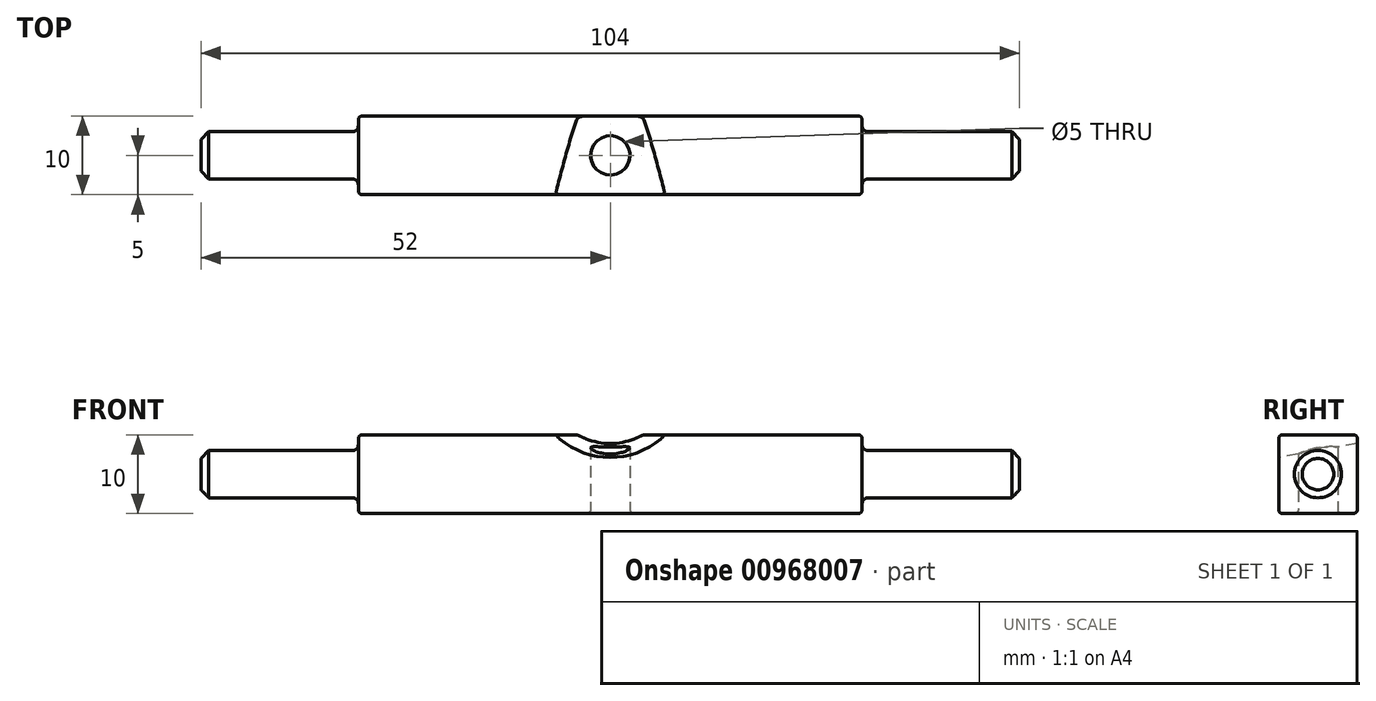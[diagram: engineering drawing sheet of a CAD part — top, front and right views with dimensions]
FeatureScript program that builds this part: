
annotation { "Feature Type Name" : "Feature", "Feature Type Description" : "" }
export const myFeature = defineFeature(function(context is Context, id is Id, definition is map)
    precondition{}
    {
        {
            var Q0;
            Q0=qCreatedBy(makeId("Right.planeOp"),FACE);
            var sketch = newSketch(context, id + "F0", { "sketchPlane" : qUnion([Q0])});
            skLineSegment(sketch, "E0.bottom", {"start": v(-5, -5) * mm, "end": v(5, -5) * mm});
            skLineSegment(sketch, "E0.top", {"start": v(-5, 5) * mm, "end": v(5, 5) * mm});
            skLineSegment(sketch, "E0.left", {"start": v(-5, -5) * mm, "end": v(-5, 5) * mm});
            skLineSegment(sketch, "E0.right", {"start": v(5, -5) * mm, "end": v(5, 5) * mm});
            skSolve(sketch);
        }
        {
            var Q0;
            Q0=makeQuery(id+"F0.imprint","IMPRINT",FACE,{"disambiguationData":[TD([[makeQuery(id+"F0.imprint","IMPRINT",EDGE,{"derivedFrom":sQuery(id+"F0.wireOp",EDGE,"E0.bottom")}),1.0]])]});
            extrude(context, id + "F1", {"entities" : qUnion([Q0]), "endBound" : BoundingType.SYMMETRIC, "depth" : 64 * mm, "offsetDistance" : 25 * mm});
        }
        {
            var Q0;
            Q0=qCreatedBy(makeId("Right.planeOp"),FACE);
            var sketch = newSketch(context, id + "F2", { "sketchPlane" : qUnion([Q0])});
            skCircle(sketch, "E1", {"center": v(0, 0) * mm, "radius": 3 * mm});
            skSolve(sketch);
        }
        {
            var Q0;
            Q0 = qSketchRegion(id + "F2", true);
            extrude(context, id + "F3", {"entities" : qUnion([Q0]), "operationType" : NewBodyOperationType.ADD, "endBound" : BoundingType.SYMMETRIC, "depth" : 104 * mm, "offsetDistance" : 25 * mm});
        }
        {
            var Q0;
            Q0=qCreatedBy(makeId("Top.planeOp"),FACE);
            var sketch = newSketch(context, id + "F4", { "sketchPlane" : qUnion([Q0])});
            skCircle(sketch, "E2", {"center": v(0, 0) * mm, "radius": 2.5 * mm});
            skSolve(sketch);
        }
        {
            var Q0;
            Q0 = qSketchRegion(id + "F4", true);
            extrude(context, id + "F5", {"entities" : qUnion([Q0]), "operationType" : NewBodyOperationType.REMOVE, "endBound" : BoundingType.SYMMETRIC, "depth" : 25 * mm, "offsetDistance" : 25 * mm});
        }
        {
            var Q0;
            Q0=makeQuery(id+"F3.opExtrude","CAP_EDGE",EDGE,{"disambiguationData":[OSD([sQuery(id+"F2.wireOp",EDGE,"E1")])],"isStart":false});
            var Q1;
            Q1=makeQuery(id+"F3.opExtrude","CAP_EDGE",EDGE,{"disambiguationData":[OSD([sQuery(id+"F2.wireOp",EDGE,"E1")])],"isStart":true});
            chamfer(context, id + "F6", {"entities" : qUnion([Q0, Q1]), "width" : 1 * mm, "tangentPropagation" : true});
        }
        {
            var Q0;
            Q0=makeQuery(id+"F1.opExtrude","SWEPT_EDGE",EDGE,{"disambiguationData":[OSD([sQuery(id+"F0.wireOp",EDGE,"E0.top"),sQuery(id+"F0.wireOp",EDGE,"E0.left")])]});
            var Q1;
            Q1=makeQuery(id+"F1.opExtrude","SWEPT_EDGE",EDGE,{"disambiguationData":[OSD([sQuery(id+"F0.wireOp",EDGE,"E0.top"),sQuery(id+"F0.wireOp",EDGE,"E0.right")])]});
            var Q2;
            Q2=makeQuery(id+"F1.opExtrude","SWEPT_EDGE",EDGE,{"disambiguationData":[OSD([sQuery(id+"F0.wireOp",EDGE,"E0.bottom"),sQuery(id+"F0.wireOp",EDGE,"E0.left")])]});
            var Q3;
            Q3=makeQuery(id+"F1.opExtrude","SWEPT_EDGE",EDGE,{"disambiguationData":[OSD([sQuery(id+"F0.wireOp",EDGE,"E0.bottom"),sQuery(id+"F0.wireOp",EDGE,"E0.right")])]});
            var Q4;
            Q4=makeQuery(id+"F1.opExtrude","CAP_EDGE",EDGE,{"disambiguationData":[OSD([sQuery(id+"F0.wireOp",EDGE,"E0.right")])],"isStart":true});
            var Q5;
            Q5=makeQuery(id+"F1.opExtrude","SWEPT_FACE",FACE,{"disambiguationData":[OSD([sQuery(id+"F0.wireOp",EDGE,"E0.bottom")])]});
            var Q6;
            Q6=makeQuery(id+"F1.opExtrude","CAP_EDGE",EDGE,{"disambiguationData":[OSD([sQuery(id+"F0.wireOp",EDGE,"E0.left")])],"isStart":true});
            var Q7;
            Q7=makeQuery(id+"F1.opExtrude","CAP_EDGE",EDGE,{"disambiguationData":[OSD([sQuery(id+"F0.wireOp",EDGE,"E0.top")])],"isStart":true});
            var Q8;
            Q8=makeQuery(id+"F1.opExtrude","CAP_EDGE",EDGE,{"disambiguationData":[OSD([sQuery(id+"F0.wireOp",EDGE,"E0.top")])],"isStart":false});
            var Q9;
            Q9=makeQuery(id+"F1.opExtrude","CAP_EDGE",EDGE,{"disambiguationData":[OSD([sQuery(id+"F0.wireOp",EDGE,"E0.left")])],"isStart":false});
            var Q10;
            Q10=makeQuery(id+"F1.opExtrude","CAP_EDGE",EDGE,{"disambiguationData":[OSD([sQuery(id+"F0.wireOp",EDGE,"E0.right")])],"isStart":false});
            fillet(context, id + "F7", {"entities" : qUnion([Q0, Q1, Q2, Q3, Q4, Q5, Q6, Q7, Q8, Q9, Q10]), "radius" : .5 * mm, "tangentPropagation" : true, "allowEdgeOverflow" : false});
        }
        {
            var Q0;
            Q0=makeQuery(id+"F3.boolean.opBoolean","INTERSECT",EDGE,{"derivedFrom":[makeQuery(id+"F1.opExtrude","CAP_FACE",FACE,{"disambiguationData":[OSD([sQuery(id+"F0.wireOp",EDGE,"E0.bottom"),sQuery(id+"F0.wireOp",EDGE,"E0.top"),sQuery(id+"F0.wireOp",EDGE,"E0.left"),sQuery(id+"F0.wireOp",EDGE,"E0.right")])],"isStart":false}),makeQuery(id+"F3.opExtrude","SWEPT_FACE",FACE,{"disambiguationData":[OSD([sQuery(id+"F2.wireOp",EDGE,"E1")])]})]});
            var Q1;
            Q1=makeQuery(id+"F3.boolean.opBoolean","INTERSECT",EDGE,{"derivedFrom":[makeQuery(id+"F1.opExtrude","CAP_FACE",FACE,{"disambiguationData":[OSD([sQuery(id+"F0.wireOp",EDGE,"E0.bottom"),sQuery(id+"F0.wireOp",EDGE,"E0.top"),sQuery(id+"F0.wireOp",EDGE,"E0.left"),sQuery(id+"F0.wireOp",EDGE,"E0.right")])],"isStart":true}),makeQuery(id+"F3.opExtrude","SWEPT_FACE",FACE,{"disambiguationData":[OSD([sQuery(id+"F2.wireOp",EDGE,"E1")])]})]});
            fillet(context, id + "F8", {"entities" : qUnion([Q0, Q1]), "radius" : .75 * mm, "tangentPropagation" : true, "allowEdgeOverflow" : false});
        }
        {
            var Q0;
            Q0=qCreatedBy(makeId("Front.planeOp"),FACE);
            var sketch = newSketch(context, id + "F9", { "sketchPlane" : qUnion([Q0])});
            skPoint(sketch, "E3.center.orphan", {"position": v(0, 12) * mm});
            skCircle(sketch, "E4", {"center": v(0, 12) * mm, "radius": 9 * mm});
            skSolve(sketch);
        }
        {
            var Q0;
            Q0 = qSketchRegion(id + "F9", true);
            extrude(context, id + "F10", {"entities" : qUnion([Q0]), "operationType" : NewBodyOperationType.REMOVE, "depth" : 25 * mm, "offsetDistance" : 25 * mm, "hasDraft" : true, "draftAngle" : 10 * degree, "hasSecondDirection" : true, "secondDirectionOppositeDirection" : true, "secondDirectionDepth" : 25 * mm, "hasSecondDirectionDraft" : true, "secondDirectionDraftAngle" : 10 * degree, "secondDirectionDraftPullDirection" : true});
        }
    });
